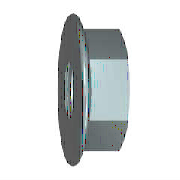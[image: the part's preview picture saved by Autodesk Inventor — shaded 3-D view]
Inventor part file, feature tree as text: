
AUTODESK INVENTOR PART (.ipt)
format: ipt  version: 2024 (Build 280153000, 153)  size: 201,728 bytes
history: native  units: mm (DEFAULTED — no unit token found)
features: other x3, extrude x1, hole x1, plane x1
ambient origin geometry x7: Origin, YZ Plane, XZ Plane, X Axis, Y Axis, Z Axis, Center Point
bodies: Solid1 (feature_tree)
feature tree (6):
  other  "Кольцо"
  extrude  "Базовый элемент"  Depth=11.8mm
  other  "Фаска1"
  hole  "Резьба"  [1 undecoded]
  other  "Work Axis1"
  plane  "Work Plane1"
note: 1 required parameter value undecoded (feature->parameter linkage not recoverable at this tier; creation-order binding heuristic only, values carry confidence <= 0.55)
